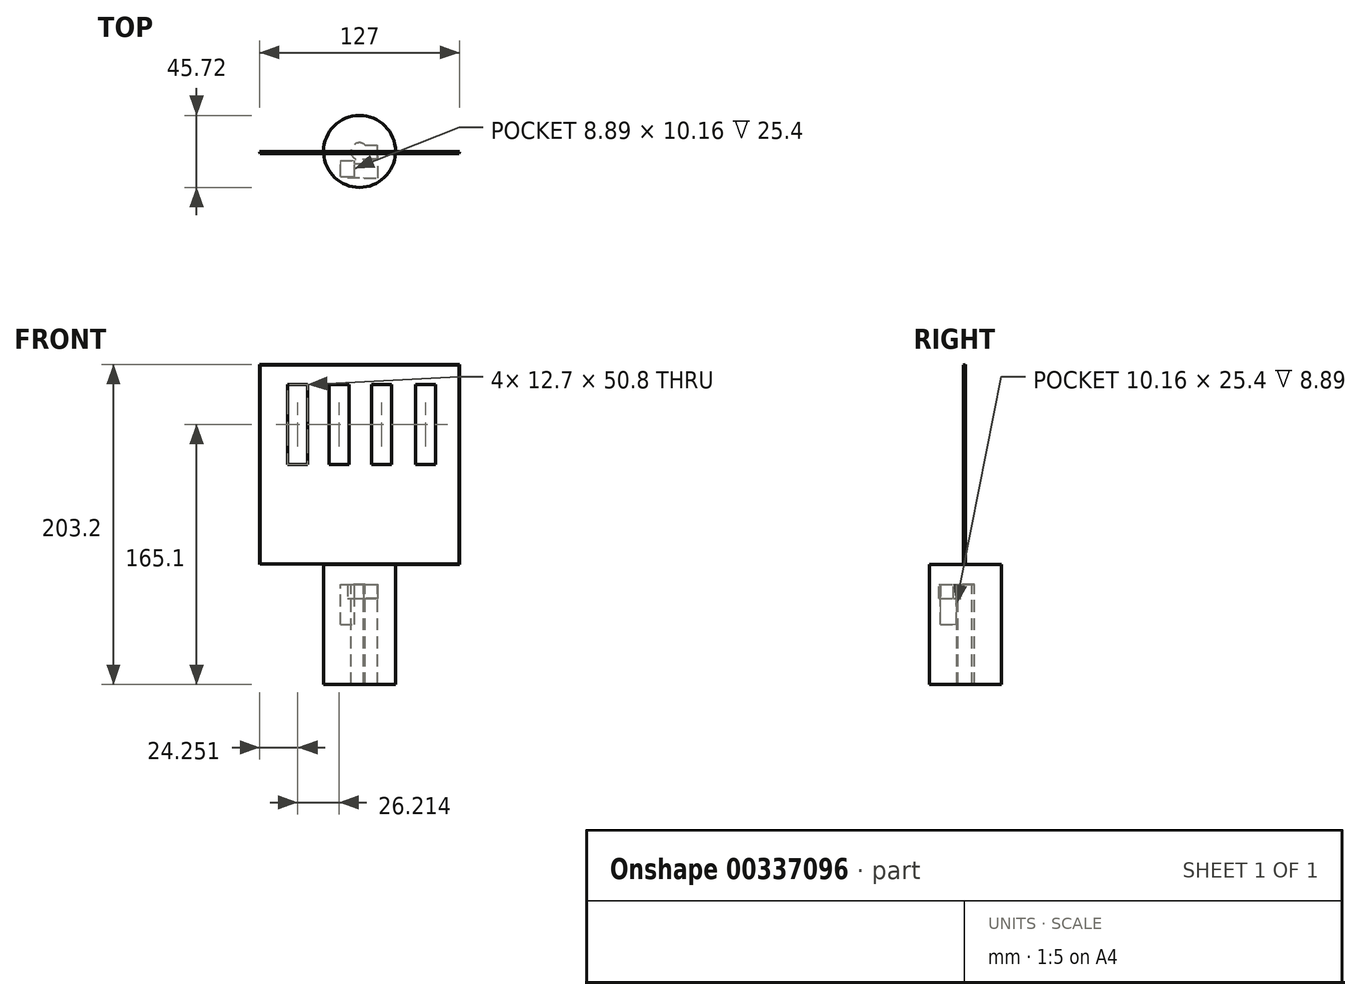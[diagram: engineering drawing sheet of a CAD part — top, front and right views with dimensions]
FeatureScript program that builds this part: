
annotation { "Feature Type Name" : "Feature", "Feature Type Description" : "" }
export const myFeature = defineFeature(function(context is Context, id is Id, definition is map)
    precondition{}
    {
        {
            var Q0;
            Q0=qCreatedBy(makeId("Front.planeOp"),FACE);
            var sketch = newSketch(context, id + "F0", { "sketchPlane" : qUnion([Q0])});
            skLineSegment(sketch, "E0.bottom", {"start": v(-63.5, 63.5) * mm, "end": v(63.5, 63.5) * mm});
            skLineSegment(sketch, "E0.top", {"start": v(-63.5, -63.5) * mm, "end": v(63.5, -63.5) * mm});
            skLineSegment(sketch, "E0.left", {"start": v(-63.5, 63.5) * mm, "end": v(-63.5, -63.5) * mm});
            skLineSegment(sketch, "E0.right", {"start": v(63.5, 63.5) * mm, "end": v(63.5, -63.5) * mm});
            skSolve(sketch);
        }
        {
            var Q0;
            Q0 = qSketchRegion(id + "F0", true);
            extrude(context, id + "F1", {"entities" : qUnion([Q0]), "depth" : 1.27 * mm, "hasDraft" : true, "draftAngle" : 10 * degree, "draftPullDirection" : true});
        }
        {
            var Q0;
            Q0=qCreatedBy(makeId("Front.planeOp"),FACE);
            var sketch = newSketch(context, id + "F2", { "sketchPlane" : qUnion([Q0])});
            skLineSegment(sketch, "E1.top", {"start": v(-45.6, 0) * mm, "end": v(-32.9, 0) * mm});
            skLineSegment(sketch, "E2", {"start": v(-45.6, 50.8) * mm, "end": v(-32.9, 50.8) * mm});
            skLineSegment(sketch, "E3", {"start": v(-32.9, 50.8) * mm, "end": v(-32.9, 0) * mm});
            skLineSegment(sketch, "E4", {"start": v(-45.6, 50.8) * mm, "end": v(-45.6, 0) * mm});
            skSolve(sketch);
        }
        {
            var Q0;
            Q0 = qSketchRegion(id + "F2", true);
            extrude(context, id + "F3", {"entities" : qUnion([Q0]), "operationType" : NewBodyOperationType.REMOVE, "depth" : 25.4 * mm});
        }
        {
            var Q0;
            Q0=qCreatedBy(makeId("Front.planeOp"),FACE);
            var sketch = newSketch(context, id + "F4", { "sketchPlane" : qUnion([Q0])});
            skLineSegment(sketch, "E5.top", {"start": v(-19.38, 0) * mm, "end": v(-6.68, 0) * mm});
            skLineSegment(sketch, "E6", {"start": v(-19.38, 50.8) * mm, "end": v(-6.68, 50.8) * mm});
            skLineSegment(sketch, "E7", {"start": v(-6.68, 50.8) * mm, "end": v(-6.68, 0) * mm});
            skLineSegment(sketch, "E8", {"start": v(-19.38, 50.8) * mm, "end": v(-19.38, 0) * mm});
            skSolve(sketch);
        }
        {
            var Q0;
            Q0 = qSketchRegion(id + "F4", true);
            extrude(context, id + "F5", {"entities" : qUnion([Q0]), "operationType" : NewBodyOperationType.REMOVE, "depth" : 25.4 * mm});
        }
        {
            var Q0;
            Q0=qCreatedBy(makeId("Front.planeOp"),FACE);
            var sketch = newSketch(context, id + "F6", { "sketchPlane" : qUnion([Q0])});
            skLineSegment(sketch, "E9.top", {"start": v(7.76, 0) * mm, "end": v(20.46, 0) * mm});
            skLineSegment(sketch, "E10", {"start": v(7.76, 50.8) * mm, "end": v(20.46, 50.8) * mm});
            skLineSegment(sketch, "E11", {"start": v(20.46, 50.8) * mm, "end": v(20.46, 0) * mm});
            skLineSegment(sketch, "E12", {"start": v(7.76, 50.8) * mm, "end": v(7.76, 0) * mm});
            skSolve(sketch);
        }
        {
            var Q0;
            Q0 = qSketchRegion(id + "F6", true);
            extrude(context, id + "F7", {"entities" : qUnion([Q0]), "operationType" : NewBodyOperationType.REMOVE, "depth" : 25.4 * mm});
        }
        {
            var Q0;
            Q0=qCreatedBy(makeId("Top.planeOp"),FACE);
            cPlane(context, id + "F8", {"entities" : qUnion([Q0]), "cplaneType" : CPlaneType.OFFSET, "offset" : 63.5 * mm, "oppositeDirection" : true, "width" : 152.4 * mm, "height" : 152.4 * mm});
        }
        {
            var Q0;
            Q0=qCreatedBy(id+"F8.planeOp",FACE);
            var sketch = newSketch(context, id + "F9", { "sketchPlane" : qUnion([Q0])});
            skCircle(sketch, "E13", {"center": v(0, 0) * mm, "radius": 22.86 * mm});
            skSolve(sketch);
        }
        {
            var Q0;
            Q0 = qSketchRegion(id + "F9", true);
            extrude(context, id + "F10", {"entities" : qUnion([Q0]), "oppositeDirection" : true, "depth" : 76.2 * mm});
        }
        {
            var Q0;
            Q0=qCreatedBy(makeId("Top.planeOp"),FACE);
            cPlane(context, id + "F11", {"entities" : qUnion([Q0]), "cplaneType" : CPlaneType.OFFSET, "offset" : 76.2 * mm, "oppositeDirection" : true, "width" : 152.4 * mm, "height" : 152.4 * mm});
        }
        {
            var Q0;
            Q0=qCreatedBy(id+"F11.planeOp",FACE);
            var sketch = newSketch(context, id + "F12", { "sketchPlane" : qUnion([Q0])});
            skCircle(sketch, "E14", {"center": v(0, 0) * mm, "radius": 5.46 * mm});
            skSolve(sketch);
        }
        {
            var Q0;
            Q0 = qSketchRegion(id + "F12", true);
            extrude(context, id + "F13", {"entities" : qUnion([Q0]), "operationType" : NewBodyOperationType.REMOVE, "oppositeDirection" : true, "depth" : 69.85 * mm});
        }
        {
            var Q0;
            Q0=qCreatedBy(id+"F11.planeOp",FACE);
            var sketch = newSketch(context, id + "F14", { "sketchPlane" : qUnion([Q0])});
            skLineSegment(sketch, "E15.bottom", {"start": v(2.72, -4.85) * mm, "end": v(11.6, -4.85) * mm});
            skLineSegment(sketch, "E15.top", {"start": v(2.72, 4.04) * mm, "end": v(11.6, 4.04) * mm});
            skLineSegment(sketch, "E15.left", {"start": v(2.72, -4.85) * mm, "end": v(2.72, 4.04) * mm});
            skLineSegment(sketch, "E15.right", {"start": v(11.6, -4.85) * mm, "end": v(11.6, 4.04) * mm});
            skSolve(sketch);
        }
        {
            var Q0;
            Q0 = qSketchRegion(id + "F14", true);
            extrude(context, id + "F15", {"entities" : qUnion([Q0]), "operationType" : NewBodyOperationType.REMOVE, "oppositeDirection" : true, "depth" : 63.5 * mm});
        }
        {
            var Q0;
            Q0=qCreatedBy(id+"F11.planeOp",FACE);
            var sketch = newSketch(context, id + "F16", { "sketchPlane" : qUnion([Q0])});
            skLineSegment(sketch, "E16.bottom", {"start": v(2.98, -16.83) * mm, "end": v(11.76, -16.83) * mm});
            skLineSegment(sketch, "E16.top", {"start": v(2.98, -3.1) * mm, "end": v(11.76, -3.1) * mm});
            skLineSegment(sketch, "E16.left", {"start": v(2.98, -16.83) * mm, "end": v(2.98, -3.1) * mm});
            skLineSegment(sketch, "E16.right", {"start": v(11.76, -16.83) * mm, "end": v(11.76, -3.1) * mm});
            skLineSegment(sketch, "E17.bottom", {"start": v(-7.56, -16.5) * mm, "end": v(3.87, -16.5) * mm});
            skLineSegment(sketch, "E17.top", {"start": v(-7.56, -7.6) * mm, "end": v(3.87, -7.6) * mm});
            skLineSegment(sketch, "E17.left", {"start": v(-7.56, -16.5) * mm, "end": v(-7.56, -7.6) * mm});
            skLineSegment(sketch, "E17.right", {"start": v(3.87, -16.5) * mm, "end": v(3.87, -7.6) * mm});
            skSolve(sketch);
        }
        {
            var Q0;
            Q0 = qSketchRegion(id + "F16", true);
            extrude(context, id + "F17", {"entities" : qUnion([Q0]), "operationType" : NewBodyOperationType.REMOVE, "oppositeDirection" : true, "depth" : 8.9 * mm});
        }
        {
            var Q0;
            Q0=qCreatedBy(id+"F11.planeOp",FACE);
            var sketch = newSketch(context, id + "F18", { "sketchPlane" : qUnion([Q0])});
            skLineSegment(sketch, "E18.bottom", {"start": v(-12.1, -15.99) * mm, "end": v(-3.2, -15.99) * mm});
            skLineSegment(sketch, "E18.top", {"start": v(-12.1, -5.83) * mm, "end": v(-3.2, -5.83) * mm});
            skLineSegment(sketch, "E18.left", {"start": v(-12.1, -15.99) * mm, "end": v(-12.1, -5.83) * mm});
            skLineSegment(sketch, "E18.right", {"start": v(-3.2, -15.99) * mm, "end": v(-3.2, -5.83) * mm});
            skSolve(sketch);
        }
        {
            var Q0;
            Q0 = qSketchRegion(id + "F18", true);
            extrude(context, id + "F19", {"entities" : qUnion([Q0]), "operationType" : NewBodyOperationType.REMOVE, "oppositeDirection" : true, "depth" : 25.4 * mm});
        }
        {
            var Q0;
            Q0=qCreatedBy(makeId("Front.planeOp"),FACE);
            var sketch = newSketch(context, id + "F20", { "sketchPlane" : qUnion([Q0])});
            skLineSegment(sketch, "E19.bottom", {"start": v(35.57, 50.8) * mm, "end": v(48.27, 50.8) * mm});
            skLineSegment(sketch, "E19.top", {"start": v(35.57, 0) * mm, "end": v(48.27, 0) * mm});
            skLineSegment(sketch, "E19.left", {"start": v(35.57, 50.8) * mm, "end": v(35.57, 0) * mm});
            skLineSegment(sketch, "E19.right", {"start": v(48.27, 50.8) * mm, "end": v(48.27, 0) * mm});
            skSolve(sketch);
        }
        {
            var Q0;
            Q0 = qSketchRegion(id + "F20", true);
            extrude(context, id + "F21", {"entities" : qUnion([Q0]), "operationType" : NewBodyOperationType.REMOVE, "depth" : 25.4 * mm});
        }
    });
